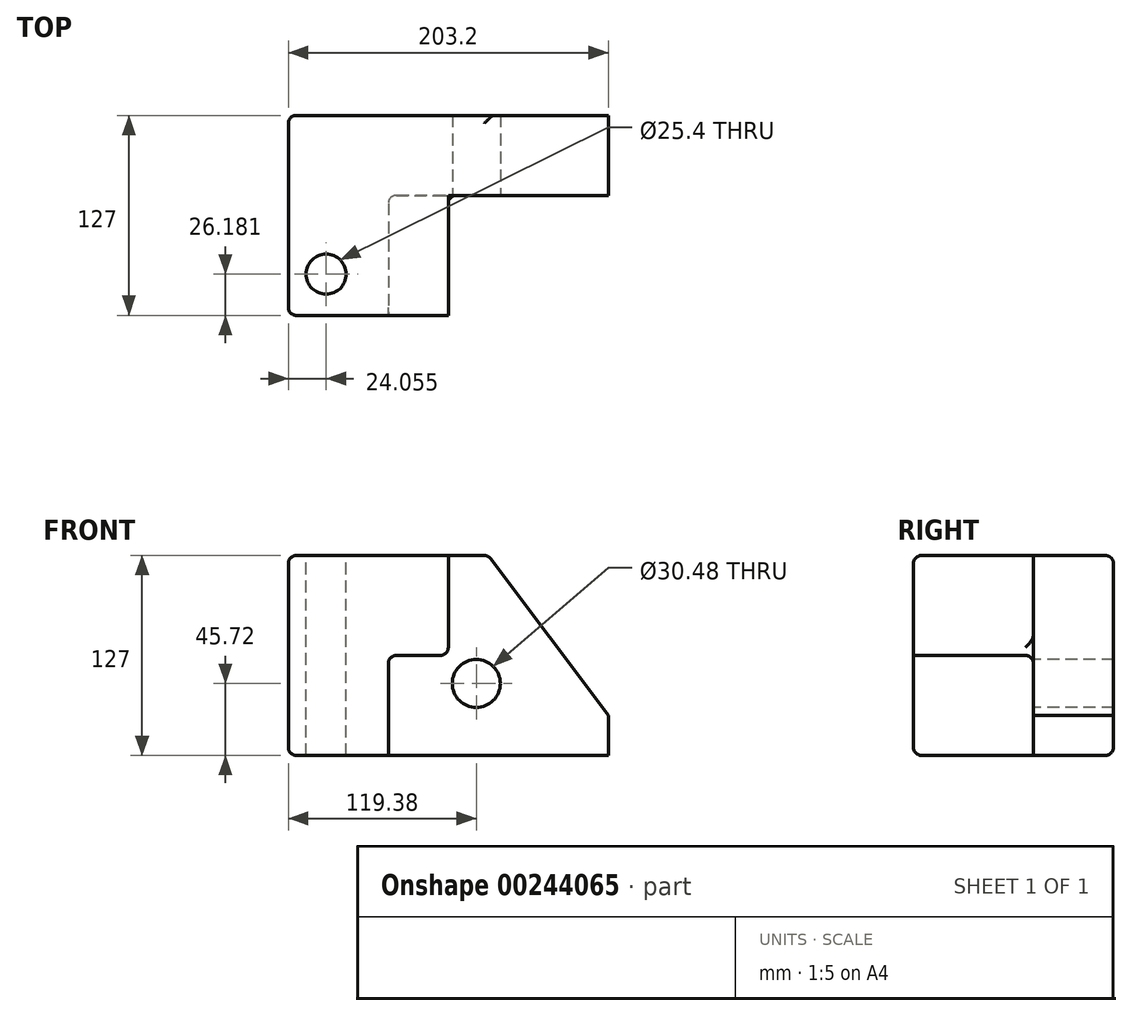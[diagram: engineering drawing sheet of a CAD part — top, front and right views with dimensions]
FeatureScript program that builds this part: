
annotation { "Feature Type Name" : "Feature", "Feature Type Description" : "" }
export const myFeature = defineFeature(function(context is Context, id is Id, definition is map)
    precondition{}
    {
        {
            var Q0;
            Q0=qCreatedBy(makeId("Front.planeOp"),FACE);
            var sketch = newSketch(context, id + "F0", { "sketchPlane" : qUnion([Q0])});
            skLineSegment(sketch, "E0.bottom", {"start": v(101.6, -63.5) * mm, "end": v(-101.6, -63.5) * mm});
            skLineSegment(sketch, "E0.top", {"start": v(101.6, 63.5) * mm, "end": v(-101.6, 63.5) * mm});
            skLineSegment(sketch, "E0.left", {"start": v(101.6, -63.5) * mm, "end": v(101.6, 63.5) * mm});
            skLineSegment(sketch, "E0.right", {"start": v(-101.6, -63.5) * mm, "end": v(-101.6, 63.5) * mm});
            skPoint(sketch, "E0.middle", {"position": v(0, 0) * mm});
            skLineSegment(sketch, "E1", {"start": v(-101.6, -63.5) * mm, "end": v(-38.1, -63.5) * mm});
            skLineSegment(sketch, "E2", {"start": v(-38.1, -63.5) * mm, "end": v(-38.1, 0) * mm});
            skLineSegment(sketch, "E3", {"start": v(-38.1, 0) * mm, "end": v(0, 0) * mm});
            skLineSegment(sketch, "E4", {"start": v(0, 0) * mm, "end": v(0, 63.5) * mm});
            skSolve(sketch);
        }
        {
            var Q0;
            Q0 = qSketchRegion(id + "F0", true);
            extrude(context, id + "F1", {"entities" : qUnion([Q0]), "depth" : 127 * mm});
        }
        {
            var Q0;
            Q0=makeQuery(id+"F1.opExtrude","CAP_FACE",FACE,{"disambiguationData":[OSD([sQuery(id+"F0.wireOp",EDGE,"E0.bottom"),sQuery(id+"F0.wireOp",EDGE,"E0.top"),sQuery(id+"F0.wireOp",EDGE,"E0.left"),sQuery(id+"F0.wireOp",EDGE,"E0.right"),sQuery(id+"F0.wireOp",EDGE,"E1")])],"isStart":false});
            var sketch = newSketch(context, id + "F2", { "sketchPlane" : qUnion([Q0])});
            skLineSegment(sketch, "E5", {"start": v(-101.6, -63.5) * mm, "end": v(-38.1, -63.5) * mm});
            skLineSegment(sketch, "E6", {"start": v(-38.1, -63.5) * mm, "end": v(-38.1, 0) * mm});
            skLineSegment(sketch, "E7", {"start": v(-38.1, 0) * mm, "end": v(0, 0) * mm});
            skLineSegment(sketch, "E8", {"start": v(0, 0) * mm, "end": v(0, 63.5) * mm});
            skSolve(sketch);
        }
        {
            var Q0;
            {var subQ2=sQuery(id+"F2.wireOp",EDGE,"E6");Q0=makeQuery(id+"F2.imprint","IMPRINT",FACE,{"disambiguationData":[TD([[makeQuery(id+"F2.imprint","IMPRINT",EDGE,{"derivedFrom":subQ2}),-1.0]])]});}
            extrude(context, id + "F3", {"entities" : qUnion([Q0]), "operationType" : NewBodyOperationType.REMOVE, "oppositeDirection" : true, "depth" : 76.2 * mm});
        }
        {
            var Q0;
            Q0=makeQuery(id+"F1.opExtrude","SWEPT_EDGE",EDGE,{"disambiguationData":[OSD([sQuery(id+"F0.wireOp",EDGE,"E0.top"),sQuery(id+"F0.wireOp",EDGE,"E0.left")])]});
            chamfer(context, id + "F4", {"entities" : qUnion([Q0]), "chamferType" : ChamferType.TWO_OFFSETS, "width1" : 76.2 * mm, "oppositeDirection" : false, "width2" : 101.6 * mm, "tangentPropagation" : true});
        }
        {
            var Q0;
            Q0=makeQuery(id+"F3.boolean.opBoolean","COPY",EDGE,{"derivedFrom":makeQuery(id+"F3.opExtrude","CAP_EDGE",EDGE,{"disambiguationData":[OSD([sQuery(id+"F0.wireOp",EDGE,"E0.top")])],"isStart":false})});
            var Q1;
            {var subQ0=sQuery(id+"F0.wireOp",EDGE,"E0.top");Q1=makeQuery(id+"F4.opChamfer","BLEND_EDGE",EDGE,{"blendedFrom":[makeQuery(id+"F1.opExtrude","SWEPT_EDGE",EDGE,{"disambiguationData":[OSD([subQ0,sQuery(id+"F0.wireOp",EDGE,"E0.left")])]}),makeQuery(id+"F1.opExtrude","SWEPT_FACE",FACE,{"disambiguationData":[OSD([subQ0])]})],"blendedInto":[makeQuery(id+"F1.opExtrude","SWEPT_FACE",FACE,{"disambiguationData":[OSD([subQ0])]})]});}
            var Q2;
            Q2=makeQuery(id+"F3.boolean.opBoolean","COPY",EDGE,{"derivedFrom":makeQuery(id+"F3.opExtrude","SWEPT_EDGE",EDGE,{"disambiguationData":[OSD([sQuery(id+"F0.wireOp",EDGE,"E0.top"),sQuery(id+"F2.wireOp",EDGE,"E8")])]})});
            var Q3;
            Q3=makeQuery(id+"F1.opExtrude","CAP_EDGE",EDGE,{"disambiguationData":[OSD([sQuery(id+"F0.wireOp",EDGE,"E0.top")])],"isStart":false});
            var Q4;
            Q4=makeQuery(id+"F3.boolean.opBoolean","COPY",EDGE,{"derivedFrom":makeQuery(id+"F3.opExtrude","CAP_EDGE",EDGE,{"disambiguationData":[OSD([sQuery(id+"F2.wireOp",EDGE,"E8")])],"isStart":true})});
            var Q5;
            Q5=makeQuery(id+"F3.boolean.opBoolean","COPY",EDGE,{"derivedFrom":makeQuery(id+"F3.opExtrude","SWEPT_EDGE",EDGE,{"disambiguationData":[OSD([sQuery(id+"F2.wireOp",EDGE,"E7"),sQuery(id+"F2.wireOp",EDGE,"E8")])]})});
            var Q6;
            Q6=makeQuery(id+"F3.boolean.opBoolean","COPY",EDGE,{"derivedFrom":makeQuery(id+"F3.opExtrude","CAP_EDGE",EDGE,{"disambiguationData":[OSD([sQuery(id+"F2.wireOp",EDGE,"E7")])],"isStart":true})});
            var Q7;
            Q7=makeQuery(id+"F3.boolean.opBoolean","COPY",EDGE,{"derivedFrom":makeQuery(id+"F3.opExtrude","CAP_EDGE",EDGE,{"disambiguationData":[OSD([sQuery(id+"F2.wireOp",EDGE,"E6")])],"isStart":true})});
            var Q8;
            Q8=makeQuery(id+"F3.boolean.opBoolean","COPY",EDGE,{"derivedFrom":makeQuery(id+"F3.opExtrude","SWEPT_EDGE",EDGE,{"disambiguationData":[OSD([sQuery(id+"F0.wireOp",EDGE,"E0.bottom"),sQuery(id+"F0.wireOp",EDGE,"E1"),sQuery(id+"F2.wireOp",EDGE,"E5"),sQuery(id+"F2.wireOp",EDGE,"E6")])]})});
            var Q9;
            Q9=makeQuery(id+"F1.opExtrude","CAP_EDGE",EDGE,{"disambiguationData":[OSD([sQuery(id+"F0.wireOp",EDGE,"E0.bottom"),sQuery(id+"F0.wireOp",EDGE,"E1")])],"isStart":false});
            var Q10;
            Q10=makeQuery(id+"F1.opExtrude","CAP_EDGE",EDGE,{"disambiguationData":[OSD([sQuery(id+"F0.wireOp",EDGE,"E0.right")])],"isStart":false});
            var Q11;
            Q11=makeQuery(id+"F1.opExtrude","SWEPT_EDGE",EDGE,{"disambiguationData":[OSD([sQuery(id+"F0.wireOp",EDGE,"E0.top"),sQuery(id+"F0.wireOp",EDGE,"E0.right")])]});
            var Q12;
            Q12=makeQuery(id+"F1.opExtrude","CAP_EDGE",EDGE,{"disambiguationData":[OSD([sQuery(id+"F0.wireOp",EDGE,"E0.top")])],"isStart":true});
            var Q13;
            Q13=makeQuery(id+"F3.boolean.opBoolean","COPY",EDGE,{"derivedFrom":makeQuery(id+"F3.opExtrude","CAP_EDGE",EDGE,{"disambiguationData":[OSD([sQuery(id+"F2.wireOp",EDGE,"E6")])],"isStart":false})});
            var Q14;
            Q14=makeQuery(id+"F3.boolean.opBoolean","COPY",EDGE,{"derivedFrom":makeQuery(id+"F3.opExtrude","SWEPT_EDGE",EDGE,{"disambiguationData":[OSD([sQuery(id+"F2.wireOp",EDGE,"E6"),sQuery(id+"F2.wireOp",EDGE,"E7")])]})});
            var Q15;
            Q15=makeQuery(id+"F3.boolean.opBoolean","COPY",EDGE,{"derivedFrom":makeQuery(id+"F3.opExtrude","CAP_EDGE",EDGE,{"disambiguationData":[OSD([sQuery(id+"F2.wireOp",EDGE,"E7")])],"isStart":false})});
            var Q16;
            Q16=makeQuery(id+"F1.opExtrude","CAP_EDGE",EDGE,{"disambiguationData":[OSD([sQuery(id+"F0.wireOp",EDGE,"E0.right")])],"isStart":true});
            var Q17;
            Q17=makeQuery(id+"F1.opExtrude","SWEPT_EDGE",EDGE,{"disambiguationData":[OSD([sQuery(id+"F0.wireOp",EDGE,"E0.right"),sQuery(id+"F0.wireOp",EDGE,"E1")])]});
            var Q18;
            Q18=makeQuery(id+"F1.opExtrude","CAP_EDGE",EDGE,{"disambiguationData":[OSD([sQuery(id+"F0.wireOp",EDGE,"E0.bottom"),sQuery(id+"F0.wireOp",EDGE,"E1")])],"isStart":true});
            fillet(context, id + "F5", {"entities" : qUnion([Q0, Q1, Q2, Q3, Q4, Q5, Q6, Q7, Q8, Q9, Q10, Q11, Q12, Q13, Q14, Q15, Q16, Q17, Q18]), "radius" : 5.08 * mm, "tangentPropagation" : true, "allowEdgeOverflow" : false});
        }
        {
            var Q0;
            Q0=makeQuery(id+"F3.boolean.opBoolean","COPY",FACE,{"derivedFrom":makeQuery(id+"F3.opExtrude","CAP_FACE",FACE,{"disambiguationData":[OSD([sQuery(id+"F0.wireOp",EDGE,"E0.bottom"),sQuery(id+"F0.wireOp",EDGE,"E0.top"),sQuery(id+"F0.wireOp",EDGE,"E0.left"),sQuery(id+"F0.wireOp",EDGE,"E1"),sQuery(id+"F2.wireOp",EDGE,"E6"),sQuery(id+"F2.wireOp",EDGE,"E7"),sQuery(id+"F2.wireOp",EDGE,"E8")])],"isStart":false})});
            var sketch = newSketch(context, id + "F6", { "sketchPlane" : qUnion([Q0])});
            skCircle(sketch, "E9", {"center": v(17.78, -17.78) * mm, "radius": 15.24 * mm});
            skSolve(sketch);
        }
        {
            var Q0;
            Q0=makeQuery(id+"F6.imprint","IMPRINT",FACE,{"disambiguationData":[TD([[makeQuery(id+"F6.imprint","IMPRINT",EDGE,{"derivedFrom":sQuery(id+"F6.wireOp",EDGE,"E9")}),1.0]])]});
            var Q1;
            Q1=makeQuery(id+"F1.opExtrude","CAP_FACE",FACE,{"disambiguationData":[OSD([sQuery(id+"F0.wireOp",EDGE,"E0.bottom"),sQuery(id+"F0.wireOp",EDGE,"E0.top"),sQuery(id+"F0.wireOp",EDGE,"E0.left"),sQuery(id+"F0.wireOp",EDGE,"E0.right"),sQuery(id+"F0.wireOp",EDGE,"E1")])],"isStart":true});
            extrude(context, id + "F7", {"entities" : qUnion([Q0]), "operationType" : NewBodyOperationType.REMOVE, "endBound" : BoundingType.UP_TO_SURFACE, "oppositeDirection" : true, "endBoundEntityFace" : qUnion([Q1]), "depth" : 25.4 * mm});
        }
        {
            var Q0;
            Q0=makeQuery(id+"F1.opExtrude","SWEPT_FACE",FACE,{"disambiguationData":[OSD([sQuery(id+"F0.wireOp",EDGE,"E0.top")])]});
            var sketch = newSketch(context, id + "F8", { "sketchPlane" : qUnion([Q0])});
            skCircle(sketch, "E10", {"center": v(-77.54, -100.82) * mm, "radius": 12.7 * mm});
            skSolve(sketch);
        }
        {
            var Q0;
            Q0=makeQuery(id+"F8.imprint","IMPRINT",FACE,{"disambiguationData":[TD([[makeQuery(id+"F8.imprint","IMPRINT",EDGE,{"derivedFrom":sQuery(id+"F8.wireOp",EDGE,"E10")}),1.0]])]});
            var Q1;
            Q1=makeQuery(id+"F1.opExtrude","SWEPT_FACE",FACE,{"disambiguationData":[OSD([sQuery(id+"F0.wireOp",EDGE,"E0.bottom"),sQuery(id+"F0.wireOp",EDGE,"E1")])]});
            extrude(context, id + "F9", {"entities" : qUnion([Q0]), "operationType" : NewBodyOperationType.REMOVE, "endBound" : BoundingType.UP_TO_SURFACE, "oppositeDirection" : true, "endBoundEntityFace" : qUnion([Q1]), "depth" : 25.4 * mm});
        }
    });
